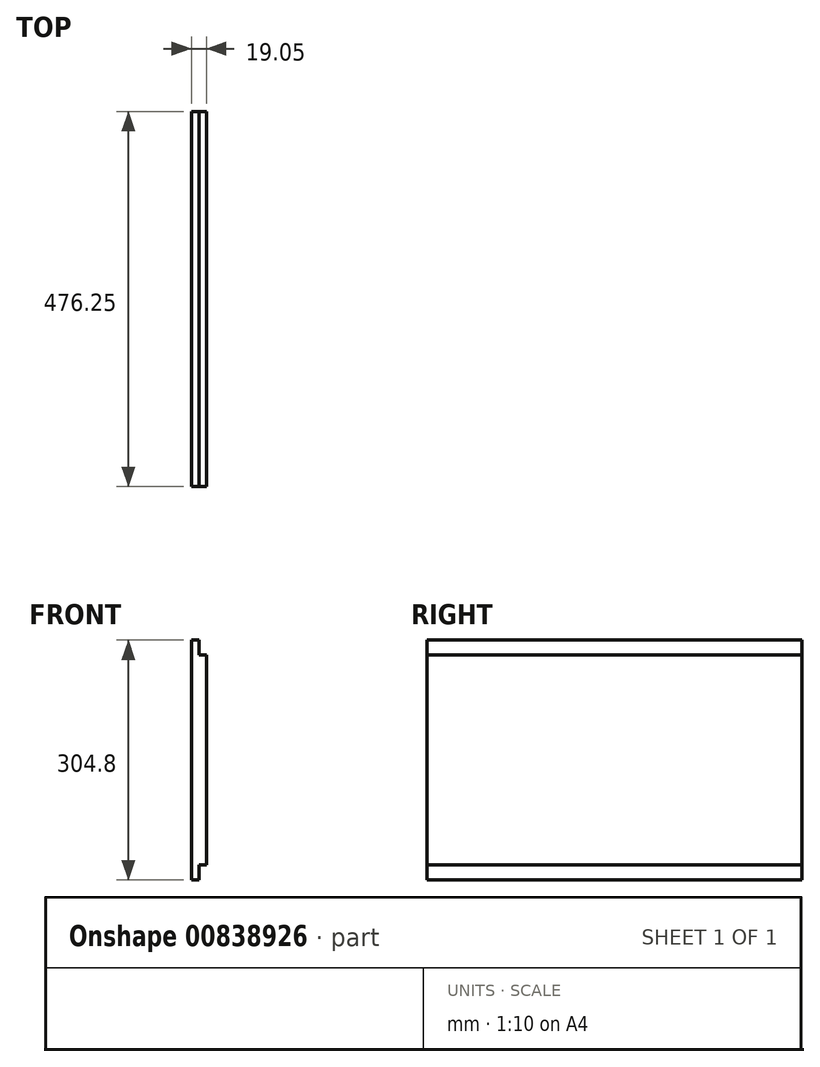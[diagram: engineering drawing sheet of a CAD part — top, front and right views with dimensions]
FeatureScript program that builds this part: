
annotation { "Feature Type Name" : "Feature", "Feature Type Description" : "" }
export const myFeature = defineFeature(function(context is Context, id is Id, definition is map)
    precondition{}
    {
        {
            var Q0;
            Q0=qCreatedBy(makeId("Front.planeOp"),FACE);
            var sketch = newSketch(context, id + "F0", { "sketchPlane" : qUnion([Q0])});
            skLineSegment(sketch, "E0", {"start": v(0, 0) * mm, "end": v(0, 304.8) * mm});
            skLineSegment(sketch, "E1", {"start": v(0, 304.8) * mm, "end": v(9.52, 304.8) * mm});
            skLineSegment(sketch, "E2", {"start": v(9.52, 304.8) * mm, "end": v(9.53, 285.75) * mm});
            skLineSegment(sketch, "E3", {"start": v(9.52, 285.75) * mm, "end": v(19.05, 285.75) * mm});
            skLineSegment(sketch, "E4", {"start": v(19.05, 285.75) * mm, "end": v(19.05, 19.05) * mm});
            skLineSegment(sketch, "E5", {"start": v(19.05, 19.05) * mm, "end": v(9.52, 19.05) * mm});
            skLineSegment(sketch, "E6", {"start": v(9.52, 19.05) * mm, "end": v(9.52, 0) * mm});
            skLineSegment(sketch, "E7", {"start": v(9.52, 0) * mm, "end": v(0, 0) * mm});
            skSolve(sketch);
        }
        {
            var Q0;
            Q0 = qSketchRegion(id + "F0", true);
            extrude(context, id + "F1", {"entities" : qUnion([Q0]), "oppositeDirection" : true, "depth" : 476.25 * mm, "offsetDistance" : 25.4 * mm});
        }
    });
